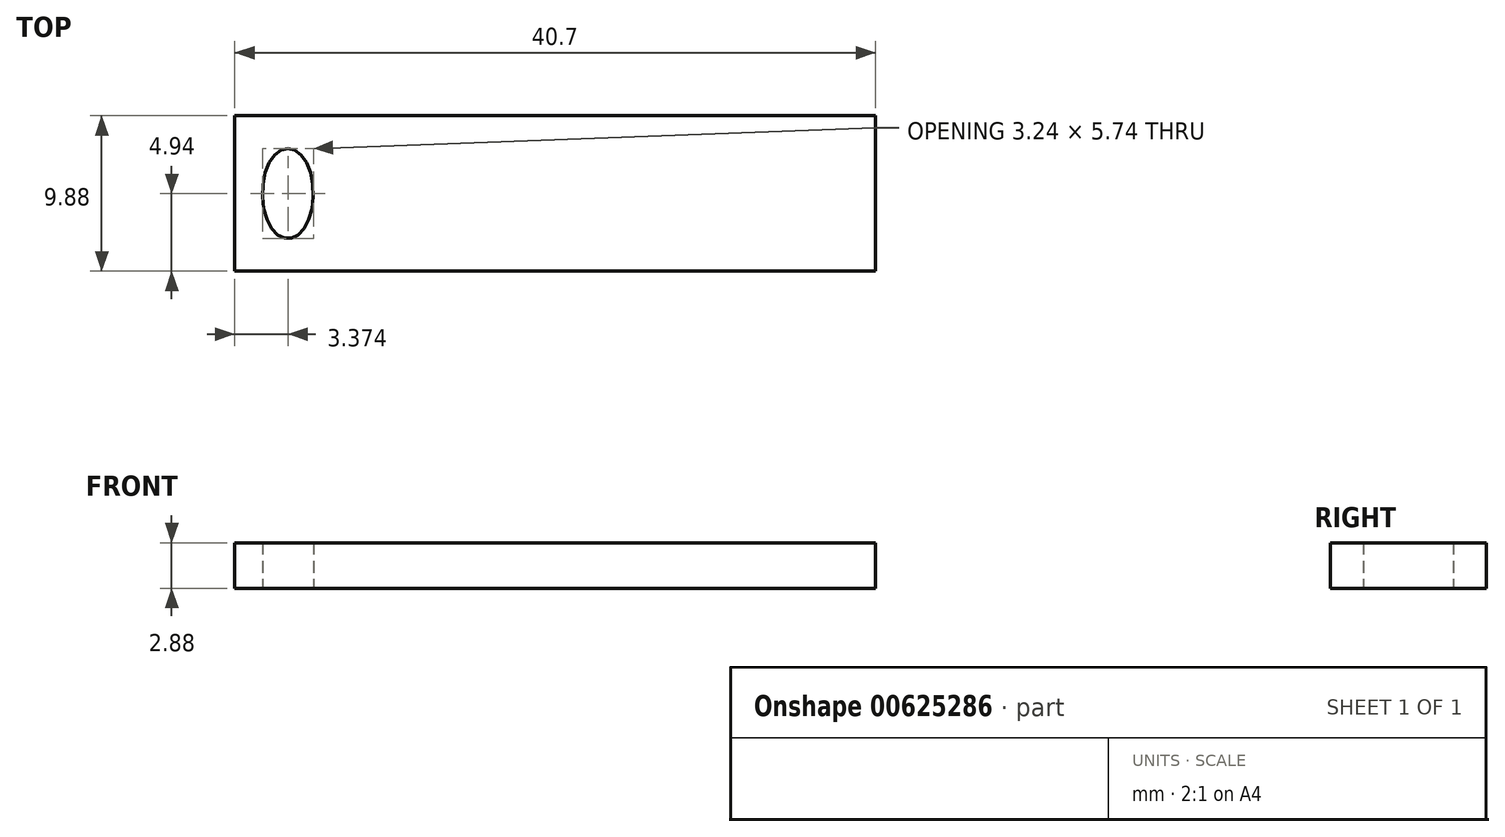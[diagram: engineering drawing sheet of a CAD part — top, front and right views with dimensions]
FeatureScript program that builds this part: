
annotation { "Feature Type Name" : "Feature", "Feature Type Description" : "" }
export const myFeature = defineFeature(function(context is Context, id is Id, definition is map)
    precondition{}
    {
        {
            var Q0;
            Q0=qCreatedBy(makeId("Top.planeOp"),FACE);
            var sketch = newSketch(context, id + "F0", { "sketchPlane" : qUnion([Q0])});
            skLineSegment(sketch, "E0.bottom", {"start": v(-20.35, 4.94) * mm, "end": v(20.35, 4.94) * mm});
            skLineSegment(sketch, "E0.top", {"start": v(-20.35, -4.94) * mm, "end": v(20.35, -4.94) * mm});
            skLineSegment(sketch, "E0.left", {"start": v(-20.35, 4.94) * mm, "end": v(-20.35, -4.94) * mm});
            skLineSegment(sketch, "E0.right", {"start": v(20.35, 4.94) * mm, "end": v(20.35, -4.94) * mm});
            skPoint(sketch, "E0.middle", {"position": v(0, 0) * mm});
            skEllipse(sketch, "E1", {"center": v(-16.98, 0) * mm, "majorRadius": 2.87 * mm, "minorRadius": 1.62 * mm, "majorAxis": v(0, 1)});
            skSolve(sketch);
        }
        {
            var Q0;
            Q0=makeQuery(id+"F0.imprint","IMPRINT",FACE,{"disambiguationData":[TD([[makeQuery(id+"F0.imprint","IMPRINT",EDGE,{"derivedFrom":sQuery(id+"F0.wireOp",EDGE,"E0.bottom")}),-1.0]])]});
            extrude(context, id + "F1", {"entities" : qUnion([Q0]), "depth" : 2.88 * mm, "offsetDistance" : 25 * mm});
        }
    });
